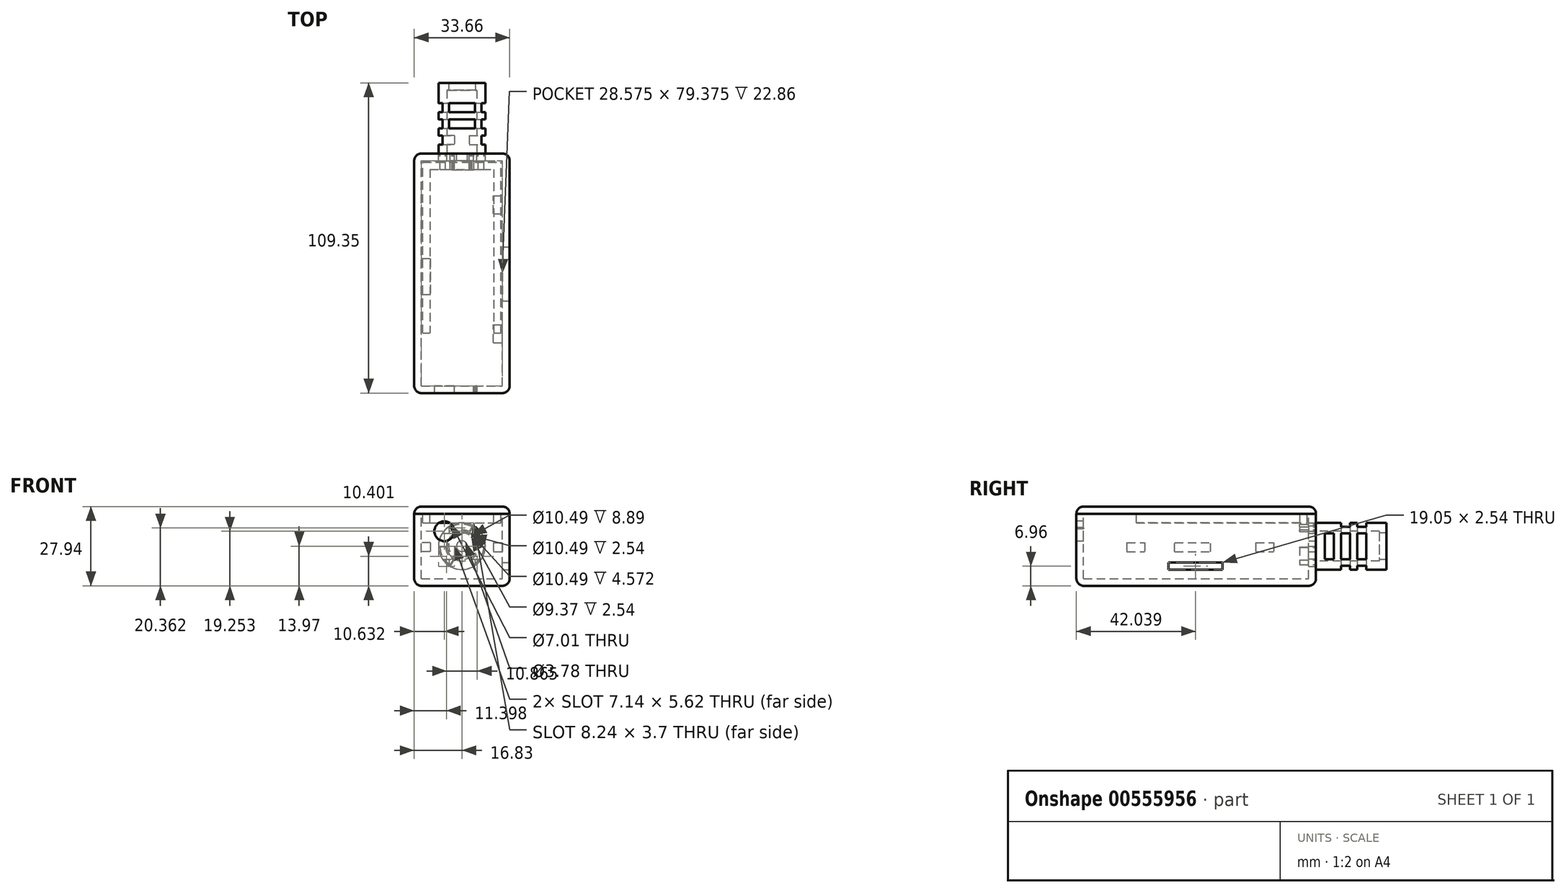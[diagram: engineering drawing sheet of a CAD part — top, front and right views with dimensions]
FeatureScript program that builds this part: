
annotation { "Feature Type Name" : "Feature", "Feature Type Description" : "" }
export const myFeature = defineFeature(function(context is Context, id is Id, definition is map)
    precondition{}
    {
        {
            var Q0;
            Q0=qCreatedBy(makeId("Top.planeOp"),FACE);
            var sketch = newSketch(context, id + "F0", { "sketchPlane" : qUnion([Q0])});
            skLineSegment(sketch, "E0.bottom", {"start": v(-14.29, -39.69) * mm, "end": v(14.29, -39.69) * mm});
            skLineSegment(sketch, "E0.top", {"start": v(-14.29, 39.69) * mm, "end": v(14.29, 39.69) * mm});
            skLineSegment(sketch, "E0.left", {"start": v(-14.29, -39.69) * mm, "end": v(-14.29, 39.69) * mm});
            skLineSegment(sketch, "E0.right", {"start": v(14.29, -39.69) * mm, "end": v(14.29, 39.69) * mm});
            skPoint(sketch, "E0.middle", {"position": v(0, 0) * mm});
            skLineSegment(sketch, "E1.0", {"start": v(-16.83, -42.23) * mm, "end": v(-16.83, 42.23) * mm});
            skLineSegment(sketch, "E1.1", {"start": v(-16.83, -42.23) * mm, "end": v(16.83, -42.23) * mm});
            skLineSegment(sketch, "E1.2", {"start": v(16.83, -42.23) * mm, "end": v(16.83, 42.23) * mm});
            skLineSegment(sketch, "E1.3", {"start": v(-16.83, 42.23) * mm, "end": v(16.83, 42.23) * mm});
            skSolve(sketch);
        }
        {
            var Q0;
            Q0=makeQuery(id+"F0.imprint","IMPRINT",FACE,{"disambiguationData":[TD([[makeQuery(id+"F0.imprint","IMPRINT",EDGE,{"derivedFrom":sQuery(id+"F0.wireOp",EDGE,"E0.bottom")}),1.0]])]});
            var Q1;
            Q1=makeQuery(id+"F0.imprint","IMPRINT",FACE,{"disambiguationData":[TD([[makeQuery(id+"F0.imprint","IMPRINT",EDGE,{"derivedFrom":sQuery(id+"F0.wireOp",EDGE,"E0.bottom")}),-1.0]])]});
            extrude(context, id + "F1", {"entities" : qUnion([Q0, Q1]), "depth" : 25.4 * mm, "offsetDistance" : 25.4 * mm});
        }
        {
            var Q0;
            Q0=makeQuery(id+"F1.opExtrude","CAP_FACE",FACE,{"disambiguationData":[OSD([sQuery(id+"F0.wireOp",EDGE,"E1.0"),sQuery(id+"F0.wireOp",EDGE,"E1.1"),sQuery(id+"F0.wireOp",EDGE,"E1.2"),sQuery(id+"F0.wireOp",EDGE,"E1.3")])],"isStart":false});
            var sketch = newSketch(context, id + "F2", { "sketchPlane" : qUnion([Q0])});
            skLineSegment(sketch, "E2.0", {"start": v(-14.29, 39.69) * mm, "end": v(14.29, 39.69) * mm});
            skLineSegment(sketch, "E3.0", {"start": v(14.29, -39.69) * mm, "end": v(14.29, 39.69) * mm});
            skLineSegment(sketch, "E4.0", {"start": v(-14.29, -39.69) * mm, "end": v(14.29, -39.69) * mm});
            skLineSegment(sketch, "E5.0", {"start": v(-14.29, -39.69) * mm, "end": v(-14.29, 39.69) * mm});
            skSolve(sketch);
        }
        {
            var Q0;
            Q0 = qSketchRegion(id + "F2", true);
            extrude(context, id + "F3", {"entities" : qUnion([Q0]), "operationType" : NewBodyOperationType.REMOVE, "oppositeDirection" : true, "depth" : 22.86 * mm, "offsetDistance" : 25.4 * mm});
        }
        {
            var Q0;
            Q0=makeQuery(id+"F1.opExtrude","SWEPT_FACE",FACE,{"disambiguationData":[OSD([sQuery(id+"F0.wireOp",EDGE,"E1.1")])]});
            var sketch = newSketch(context, id + "F4", { "sketchPlane" : qUnion([Q0])});
            skCircle(sketch, "E6", {"center": v(-6.2, 19.25) * mm, "radius": 3.5 * mm});
            skLineSegment(sketch, "E7", {"start": v(-16.83, 19.25) * mm, "end": v(-6.2, 19.25) * mm, "construction": true});
            skLineSegment(sketch, "E8", {"start": v(-6.2, 19.25) * mm, "end": v(-6.2, 0) * mm, "construction": true});
            skLineSegment(sketch, "E9", {"start": v(-16.83, 16.76) * mm, "end": v(16.83, 16.76) * mm, "construction": true});
            skLineSegment(sketch, "E10", {"start": v(0, 16.76) * mm, "end": v(0, 0) * mm, "construction": true});
            skLineSegment(sketch, "E11", {"start": v(5.8, 20.03) * mm, "end": v(8.1, 20.03) * mm});
            skPoint(sketch, "E12", {"position": v(5.8, 20.03) * mm});
            skLineSegment(sketch, "E13", {"start": v(6.32, 21.08) * mm, "end": v(8.95, 21.08) * mm});
            skPoint(sketch, "E14", {"position": v(6.32, 21.08) * mm});
            skLineSegment(sketch, "E15", {"start": v(6.32, 17.98) * mm, "end": v(8.44, 17.98) * mm});
            skPoint(sketch, "E16", {"position": v(6.32, 17.98) * mm});
            skLineSegment(sketch, "E17", {"start": v(6.32, 18.43) * mm, "end": v(8.07, 18.43) * mm});
            skPoint(sketch, "E18", {"position": v(6.32, 18.43) * mm});
            skPoint(sketch, "E19", {"position": v(5.8, 21.48) * mm});
            skPoint(sketch, "E20", {"position": v(5.8, 17.58) * mm});
            skArc(sketch, "E21", {"start": v(9.25, 20.78) * mm, "mid": v(9.17, 21) * mm, "end": v(8.95, 21.08) * mm});
            skLineSegment(sketch, "E22", {"start": v(9.25, 20.78) * mm, "end": v(9.25, 20.21) * mm});
            skArc(sketch, "E23", {"start": v(8.95, 19.64) * mm, "mid": v(9.17, 19.89) * mm, "end": v(9.25, 20.21) * mm});
            skArc(sketch, "E24", {"start": v(8.95, 19.64) * mm, "mid": v(8.8, 19.4) * mm, "end": v(8.74, 19.13) * mm});
            skArc(sketch, "E25", {"start": v(8.44, 17.98) * mm, "mid": v(8.65, 18.07) * mm, "end": v(8.74, 18.28) * mm});
            skLineSegment(sketch, "E26", {"start": v(8.74, 19.13) * mm, "end": v(8.74, 18.28) * mm});
            skLineSegment(sketch, "E27", {"start": v(8.1, 20.03) * mm, "end": v(8.1, 19.13) * mm});
            skLineSegment(sketch, "E28", {"start": v(8.1, 19.13) * mm, "end": v(8.07, 18.43) * mm});
            skLineSegment(sketch, "E29", {"start": v(5.8, 21.48) * mm, "end": v(5.8, 17.58) * mm, "construction": true});
            skLineSegment(sketch, "E30.bottom", {"start": v(7.15, 20.03) * mm, "end": v(7.65, 20.03) * mm});
            skLineSegment(sketch, "E30.top", {"start": v(7.15, 20.53) * mm, "end": v(7.65, 20.53) * mm});
            skLineSegment(sketch, "E30.left", {"start": v(7.15, 20.03) * mm, "end": v(7.15, 20.53) * mm});
            skLineSegment(sketch, "E30.right", {"start": v(7.65, 20.03) * mm, "end": v(7.65, 20.53) * mm});
            skPoint(sketch, "E30.middle", {"position": v(7.4, 20.28) * mm});
            skLineSegment(sketch, "E31.bottom", {"start": v(6.85, 20.03) * mm, "end": v(6.35, 20.03) * mm});
            skLineSegment(sketch, "E31.top", {"start": v(6.85, 20.53) * mm, "end": v(6.35, 20.53) * mm});
            skLineSegment(sketch, "E31.left", {"start": v(6.85, 20.03) * mm, "end": v(6.85, 20.53) * mm});
            skLineSegment(sketch, "E31.right", {"start": v(6.35, 20.03) * mm, "end": v(6.35, 20.53) * mm});
            skPoint(sketch, "E31.middle", {"position": v(6.6, 20.28) * mm});
            skLineSegment(sketch, "E32", {"start": v(6.05, 20.53) * mm, "end": v(6.05, 20.03) * mm});
            skLineSegment(sketch, "E33", {"start": v(6.32, 20.53) * mm, "end": v(6.05, 20.53) * mm});
            skLineSegment(sketch, "E34", {"start": v(5.8, 17.58) * mm, "end": v(8.44, 17.58) * mm});
            skLineSegment(sketch, "E35", {"start": v(5.8, 21.48) * mm, "end": v(8.95, 21.48) * mm});
            skArc(sketch, "E36", {"start": v(9.65, 20.78) * mm, "mid": v(9.45, 21.28) * mm, "end": v(8.95, 21.48) * mm});
            skLineSegment(sketch, "E37", {"start": v(9.65, 20.78) * mm, "end": v(9.65, 20.21) * mm});
            skArc(sketch, "E38", {"start": v(9.25, 19.36) * mm, "mid": v(9.55, 19.74) * mm, "end": v(9.65, 20.21) * mm});
            skArc(sketch, "E39", {"start": v(9.25, 19.36) * mm, "mid": v(9.17, 19.26) * mm, "end": v(9.14, 19.13) * mm});
            skLineSegment(sketch, "E40", {"start": v(9.14, 19.13) * mm, "end": v(9.14, 18.28) * mm});
            skArc(sketch, "E41", {"start": v(8.44, 17.58) * mm, "mid": v(8.94, 17.78) * mm, "end": v(9.14, 18.28) * mm});
            skArc(sketch, "E42.MirrorCS", {"start": v(2.35, 19.36) * mm, "mid": v(2.44, 19.26) * mm, "end": v(2.46, 19.13) * mm});
            skLineSegment(sketch, "E43.MirrorCS", {"start": v(4.45, 20.03) * mm, "end": v(3.95, 20.03) * mm});
            skLineSegment(sketch, "E44.MirrorCS", {"start": v(4.45, 20.03) * mm, "end": v(4.45, 20.53) * mm});
            skLineSegment(sketch, "E45.MirrorCS", {"start": v(4.75, 20.03) * mm, "end": v(5.25, 20.03) * mm});
            skLineSegment(sketch, "E46.MirrorCS", {"start": v(5.25, 20.03) * mm, "end": v(5.25, 20.53) * mm});
            skLineSegment(sketch, "E47.MirrorCS", {"start": v(5.55, 20.53) * mm, "end": v(5.55, 20.03) * mm});
            skLineSegment(sketch, "E48.MirrorCS", {"start": v(5.29, 20.53) * mm, "end": v(5.55, 20.53) * mm});
            skLineSegment(sketch, "E49.MirrorCS", {"start": v(4.45, 20.53) * mm, "end": v(3.95, 20.53) * mm});
            skArc(sketch, "E50.MirrorCS", {"start": v(3.17, 17.58) * mm, "mid": v(2.67, 17.78) * mm, "end": v(2.46, 18.28) * mm});
            skPoint(sketch, "E51.MirrorP", {"position": v(5.29, 18.43) * mm});
            skLineSegment(sketch, "E52.MirrorCS", {"start": v(5.29, 17.98) * mm, "end": v(3.17, 17.98) * mm});
            skLineSegment(sketch, "E53.MirrorCS", {"start": v(5.8, 21.48) * mm, "end": v(2.65, 21.48) * mm});
            skLineSegment(sketch, "E54.MirrorCS", {"start": v(5.29, 18.43) * mm, "end": v(3.53, 18.43) * mm});
            skPoint(sketch, "E55.MirrorP", {"position": v(4.2, 20.28) * mm});
            skArc(sketch, "E56.MirrorCS", {"start": v(1.95, 20.78) * mm, "mid": v(2.16, 21.28) * mm, "end": v(2.65, 21.48) * mm});
            skLineSegment(sketch, "E57.MirrorCS", {"start": v(4.75, 20.03) * mm, "end": v(4.75, 20.53) * mm});
            skPoint(sketch, "E58.MirrorP", {"position": v(5.29, 17.98) * mm});
            skLineSegment(sketch, "E59.MirrorCS", {"start": v(5.29, 21.08) * mm, "end": v(2.65, 21.08) * mm});
            skLineSegment(sketch, "E60.MirrorCS", {"start": v(3.5, 19.13) * mm, "end": v(3.53, 18.43) * mm});
            skLineSegment(sketch, "E61.MirrorCS", {"start": v(2.46, 19.13) * mm, "end": v(2.46, 18.28) * mm});
            skLineSegment(sketch, "E62.MirrorCS", {"start": v(4.75, 20.53) * mm, "end": v(5.25, 20.53) * mm});
            skArc(sketch, "E63.MirrorCS", {"start": v(2.35, 20.78) * mm, "mid": v(2.44, 21) * mm, "end": v(2.65, 21.08) * mm});
            skLineSegment(sketch, "E64.MirrorCS", {"start": v(1.95, 20.78) * mm, "end": v(1.95, 20.21) * mm});
            skArc(sketch, "E65.MirrorCS", {"start": v(2.65, 19.64) * mm, "mid": v(2.43, 19.89) * mm, "end": v(2.35, 20.21) * mm});
            skLineSegment(sketch, "E66.MirrorCS", {"start": v(5.8, 20.03) * mm, "end": v(3.5, 20.03) * mm});
            skLineSegment(sketch, "E67.MirrorCS", {"start": v(2.87, 19.13) * mm, "end": v(2.87, 18.28) * mm});
            skLineSegment(sketch, "E68.MirrorCS", {"start": v(3.5, 20.03) * mm, "end": v(3.5, 19.13) * mm});
            skLineSegment(sketch, "E69.MirrorCS", {"start": v(5.8, 17.58) * mm, "end": v(3.17, 17.58) * mm});
            skPoint(sketch, "E70.MirrorP", {"position": v(5.29, 21.08) * mm});
            skLineSegment(sketch, "E71.MirrorCS", {"start": v(2.35, 20.78) * mm, "end": v(2.35, 20.21) * mm});
            skArc(sketch, "E72.MirrorCS", {"start": v(3.17, 17.98) * mm, "mid": v(2.96, 18.07) * mm, "end": v(2.87, 18.28) * mm});
            skLineSegment(sketch, "E73.MirrorCS", {"start": v(3.95, 20.03) * mm, "end": v(3.95, 20.53) * mm});
            skPoint(sketch, "E74.MirrorP", {"position": v(5, 20.28) * mm});
            skArc(sketch, "E75.MirrorCS", {"start": v(2.35, 19.36) * mm, "mid": v(2.06, 19.74) * mm, "end": v(1.95, 20.21) * mm});
            skArc(sketch, "E76.MirrorCS", {"start": v(2.65, 19.64) * mm, "mid": v(2.81, 19.4) * mm, "end": v(2.87, 19.13) * mm});
            skLineSegment(sketch, "E77", {"start": v(-16.83, 18.75) * mm, "end": v(5.8, 18.75) * mm, "construction": true});
            skLineSegment(sketch, "E78", {"start": v(5.8, 19.53) * mm, "end": v(-16.83, 19.53) * mm, "construction": true});
            skLineSegment(sketch, "E79", {"start": v(5.8, 17.58) * mm, "end": v(5.8, 0) * mm, "construction": true});
            skSolve(sketch);
        }
        {
            var Q0;
            Q0=makeQuery(id+"F4.imprint","IMPRINT",FACE,{"disambiguationData":[TD([[makeQuery(id+"F4.imprint","IMPRINT",EDGE,{"derivedFrom":sQuery(id+"F4.wireOp",EDGE,"E6")}),1.0]])]});
            var Q1;
            Q1=makeQuery(id+"F4.imprint","IMPRINT",FACE,{"disambiguationData":[TD([[makeQuery(id+"F4.imprint","IMPRINT",EDGE,{"derivedFrom":sQuery(id+"F4.wireOp",EDGE,"E30.bottom")}),-1.0]])]});
            var Q2;
            {var subQ0=sQuery(id+"F4.wireOp",EDGE,"E46.MirrorCS");Q2=makeQuery(id+"F4.imprint","IMPRINT",FACE,{"disambiguationData":[TD([[makeQuery(id+"F4.imprint","IMPRINT",EDGE,{"derivedFrom":subQ0}),1.0]])]});}
            var Q3;
            Q3=makeQuery(id+"F4.imprint","IMPRINT",FACE,{"disambiguationData":[TD([[makeQuery(id+"F4.imprint","IMPRINT",EDGE,{"derivedFrom":sQuery(id+"F4.wireOp",EDGE,"E30.bottom")}),1.0]])]});
            var Q4;
            Q4=makeQuery(id+"F4.imprint","IMPRINT",FACE,{"disambiguationData":[TD([[makeQuery(id+"F4.imprint","IMPRINT",EDGE,{"derivedFrom":sQuery(id+"F4.wireOp",EDGE,"E31.bottom")}),-1.0]])]});
            var Q5;
            {var subQ0=sQuery(id+"F4.wireOp",EDGE,"E44.MirrorCS");Q5=makeQuery(id+"F4.imprint","IMPRINT",FACE,{"disambiguationData":[TD([[makeQuery(id+"F4.imprint","IMPRINT",EDGE,{"derivedFrom":subQ0}),1.0]])]});}
            extrude(context, id + "F5", {"entities" : qUnion([Q0, Q1, Q2, Q3, Q4, Q5]), "operationType" : NewBodyOperationType.REMOVE, "endBound" : BoundingType.UP_TO_NEXT, "oppositeDirection" : true, "depth" : 25.4 * mm, "offsetDistance" : 25.4 * mm});
        }
        {
            var Q0;
            Q0=makeQuery(id+"F1.opExtrude","SWEPT_FACE",FACE,{"disambiguationData":[OSD([sQuery(id+"F0.wireOp",EDGE,"E1.2")])]});
            var sketch = newSketch(context, id + "F6", { "sketchPlane" : qUnion([Q0])});
            skLineSegment(sketch, "E80", {"start": v(-42.23, 6.96) * mm, "end": v(-0.2, 6.96) * mm, "construction": true});
            skLineSegment(sketch, "E81", {"start": v(-17.06, 6.96) * mm, "end": v(-17.06, 0) * mm, "construction": true});
            skLineSegment(sketch, "E82.bottom", {"start": v(9.33, 5.69) * mm, "end": v(-9.72, 5.69) * mm});
            skLineSegment(sketch, "E82.top", {"start": v(9.33, 8.23) * mm, "end": v(-9.72, 8.23) * mm});
            skLineSegment(sketch, "E82.left", {"start": v(9.33, 5.69) * mm, "end": v(9.33, 8.23) * mm});
            skLineSegment(sketch, "E82.right", {"start": v(-9.72, 5.69) * mm, "end": v(-9.72, 8.23) * mm});
            skPoint(sketch, "E82.middle", {"position": v(-0.2, 6.96) * mm});
            skLineSegment(sketch, "E83", {"start": v(-42.23, 15.16) * mm, "end": v(42.23, 15.16) * mm, "construction": true});
            skLineSegment(sketch, "E84", {"start": v(-0.2, 6.96) * mm, "end": v(-0.2, 15.16) * mm, "construction": true});
            skLineSegment(sketch, "E85.bottom", {"start": v(-24.44, 15.16) * mm, "end": v(-18.09, 15.16) * mm});
            skLineSegment(sketch, "E85.top", {"start": v(-24.44, 11.99) * mm, "end": v(-18.09, 11.99) * mm});
            skLineSegment(sketch, "E85.left", {"start": v(-24.44, 15.16) * mm, "end": v(-24.44, 11.99) * mm});
            skLineSegment(sketch, "E85.right", {"start": v(-18.09, 15.16) * mm, "end": v(-18.09, 11.99) * mm});
            skLineSegment(sketch, "E86.bottom", {"start": v(20.98, 15.16) * mm, "end": v(27.33, 15.16) * mm});
            skLineSegment(sketch, "E86.top", {"start": v(20.98, 11.99) * mm, "end": v(27.33, 11.99) * mm});
            skLineSegment(sketch, "E86.left", {"start": v(20.98, 15.16) * mm, "end": v(20.98, 11.99) * mm});
            skLineSegment(sketch, "E86.right", {"start": v(27.33, 15.16) * mm, "end": v(27.33, 11.99) * mm});
            skLineSegment(sketch, "E87", {"start": v(15.27, 15.16) * mm, "end": v(15.27, 0) * mm, "construction": true});
            skSolve(sketch);
        }
        {
            var Q0;
            Q0=makeQuery(id+"F6.imprint","IMPRINT",FACE,{"disambiguationData":[TD([[makeQuery(id+"F6.imprint","IMPRINT",EDGE,{"derivedFrom":sQuery(id+"F6.wireOp",EDGE,"E82.bottom")}),-1.0]])]});
            extrude(context, id + "F7", {"entities" : qUnion([Q0]), "operationType" : NewBodyOperationType.REMOVE, "oppositeDirection" : true, "depth" : 5.08 * mm, "offsetDistance" : 25.4 * mm});
        }
        {
            var Q0;
            Q0=makeQuery(id+"F2.imprint","IMPRINT",FACE,{"disambiguationData":[TD([[makeQuery(id+"F2.imprint","IMPRINT",EDGE,{"derivedFrom":sQuery(id+"F2.wireOp",EDGE,"E2.0")}),-1.0]])]});
            var sketch = newSketch(context, id + "F8", { "sketchPlane" : qUnion([Q0])});
            skLineSegment(sketch, "E88.0", {"start": v(-16.83, 42.23) * mm, "end": v(16.83, 42.23) * mm});
            skLineSegment(sketch, "E89.0", {"start": v(16.83, -42.23) * mm, "end": v(16.83, 42.23) * mm});
            skPoint(sketch, "E90.0", {"position": v(0, -42.23) * mm});
            skLineSegment(sketch, "E91.0", {"start": v(-16.83, -42.23) * mm, "end": v(-16.83, 42.23) * mm});
            skLineSegment(sketch, "E92.0", {"start": v(-14.29, -39.69) * mm, "end": v(-14.29, 39.69) * mm});
            skLineSegment(sketch, "E93.0", {"start": v(-14.29, 39.69) * mm, "end": v(14.29, 39.69) * mm});
            skLineSegment(sketch, "E94.0", {"start": v(14.29, -39.69) * mm, "end": v(14.29, 39.69) * mm});
            skLineSegment(sketch, "E95.0", {"start": v(-14.29, -39.69) * mm, "end": v(14.29, -39.69) * mm});
            skLineSegment(sketch, "E96.0", {"start": v(-13.78, 39.18) * mm, "end": v(13.78, 39.18) * mm});
            skLineSegment(sketch, "E96.1", {"start": v(-13.78, -39.18) * mm, "end": v(-13.78, 39.18) * mm});
            skLineSegment(sketch, "E96.2", {"start": v(-13.78, -39.18) * mm, "end": v(13.78, -39.18) * mm});
            skLineSegment(sketch, "E96.3", {"start": v(13.78, -39.18) * mm, "end": v(13.78, 39.18) * mm});
            skLineSegment(sketch, "E97.0.0", {"start": v(-14.29, 39.69) * mm, "end": v(-14.29, -39.69) * mm});
            skLineSegment(sketch, "E97.0.3", {"start": v(14.29, 39.69) * mm, "end": v(-14.29, 39.69) * mm});
            skSolve(sketch);
        }
        {
            var Q0;
            Q0=makeQuery(id+"F2.imprint","IMPRINT",FACE,{"disambiguationData":[TD([[makeQuery(id+"F2.imprint","IMPRINT",EDGE,{"derivedFrom":sQuery(id+"F2.wireOp",EDGE,"E2.0")}),1.0]])]});
            var Q1;
            Q1=makeQuery(id+"F2.imprint","IMPRINT",FACE,{"disambiguationData":[TD([[makeQuery(id+"F2.imprint","IMPRINT",EDGE,{"derivedFrom":sQuery(id+"F2.wireOp",EDGE,"E2.0")}),-1.0]])]});
            extrude(context, id + "F9", {"entities" : qUnion([Q0, Q1]), "depth" : 2.54 * mm, "offsetDistance" : 25.4 * mm});
        }
        {
            var Q0;
            Q0=makeQuery(id+"F8.imprint","IMPRINT",FACE,{"disambiguationData":[TD([[makeQuery(id+"F8.imprint","IMPRINT",EDGE,{"derivedFrom":sQuery(id+"F8.wireOp",EDGE,"E96.0")}),-1.0]])]});
            var sketch = newSketch(context, id + "F10", { "sketchPlane" : qUnion([Q0])});
            skLineSegment(sketch, "E98.0", {"start": v(11.24, -39.18) * mm, "end": v(11.24, 36.64) * mm, "construction": true});
            skLineSegment(sketch, "E98.1", {"start": v(-11.24, 36.64) * mm, "end": v(11.24, 36.64) * mm, "construction": true});
            skLineSegment(sketch, "E98.2", {"start": v(-11.24, -39.18) * mm, "end": v(-11.24, 36.64) * mm, "construction": true});
            skLineSegment(sketch, "E99.0", {"start": v(-13.78, 39.18) * mm, "end": v(13.78, 39.18) * mm, "construction": true});
            skLineSegment(sketch, "E100.0", {"start": v(-13.78, -39.18) * mm, "end": v(-13.78, 39.18) * mm, "construction": true});
            skLineSegment(sketch, "E101.0", {"start": v(13.78, -39.18) * mm, "end": v(13.78, 39.18) * mm, "construction": true});
            skLineSegment(sketch, "E102", {"start": v(-16.83, -21.1) * mm, "end": v(16.83, -21.1) * mm, "construction": true});
            skLineSegment(sketch, "E103", {"start": v(-13.78, -21.1) * mm, "end": v(-11.24, -21.1) * mm});
            skLineSegment(sketch, "E104", {"start": v(11.24, -21.1) * mm, "end": v(13.78, -21.1) * mm});
            skLineSegment(sketch, "E105", {"start": v(-13.78, 39.18) * mm, "end": v(-13.78, -21.1) * mm});
            skLineSegment(sketch, "E106", {"start": v(-11.24, 36.64) * mm, "end": v(-11.24, -21.1) * mm});
            skLineSegment(sketch, "E107", {"start": v(-13.78, 39.18) * mm, "end": v(13.78, 39.18) * mm});
            skLineSegment(sketch, "E108", {"start": v(-11.24, 36.64) * mm, "end": v(11.24, 36.64) * mm});
            skLineSegment(sketch, "E109", {"start": v(11.24, 36.64) * mm, "end": v(11.24, -21.1) * mm});
            skLineSegment(sketch, "E110", {"start": v(13.78, 39.18) * mm, "end": v(13.78, -21.1) * mm});
            skSolve(sketch);
        }
        {
            var Q0;
            Q0=makeQuery(id+"F10.imprint","IMPRINT",FACE,{"disambiguationData":[TD([[makeQuery(id+"F10.imprint","IMPRINT",EDGE,{"derivedFrom":sQuery(id+"F10.wireOp",EDGE,"E103")}),1.0]])]});
            var Q1;
            Q1=sQuery(id+"F10.wireOp",EDGE,"E105");
            var Q2;
            Q2=sQuery(id+"F10.wireOp",EDGE,"E107");
            var Q3;
            Q3=sQuery(id+"F10.wireOp",EDGE,"E110");
            var Q4;
            Q4=sQuery(id+"F10.wireOp",EDGE,"E103");
            var Q5;
            Q5=sQuery(id+"F10.wireOp",EDGE,"E106");
            var Q6;
            Q6=sQuery(id+"F10.wireOp",EDGE,"E104");
            var Q7;
            Q7=sQuery(id+"F10.wireOp",EDGE,"E109");
            var Q8;
            Q8=sQuery(id+"F10.wireOp",EDGE,"E108");
            extrude(context, id + "F11", {"entities" : qUnion([Q0]), "operationType" : NewBodyOperationType.ADD, "surfaceEntities" : qUnion([Q1, Q2, Q3, Q4, Q5, Q6, Q7, Q8]), "oppositeDirection" : true, "depth" : 3.17 * mm, "offsetDistance" : 25.4 * mm});
        }
        {
            var Q0;
            Q0=makeQuery(id+"F6.imprint","IMPRINT",FACE,{"disambiguationData":[TD([[makeQuery(id+"F6.imprint","IMPRINT",EDGE,{"derivedFrom":sQuery(id+"F6.wireOp",EDGE,"E86.bottom")}),-1.0]])]});
            var Q1;
            Q1=makeQuery(id+"F6.imprint","IMPRINT",FACE,{"disambiguationData":[TD([[makeQuery(id+"F6.imprint","IMPRINT",EDGE,{"derivedFrom":sQuery(id+"F6.wireOp",EDGE,"E85.bottom")}),-1.0]])]});
            extrude(context, id + "F12", {"entities" : qUnion([Q0, Q1]), "operationType" : NewBodyOperationType.ADD, "oppositeDirection" : true, "depth" : 5.7 * mm, "offsetDistance" : 25.4 * mm});
        }
        {
            var Q0;
            Q0=makeQuery(id+"F1.opExtrude","SWEPT_FACE",FACE,{"disambiguationData":[OSD([sQuery(id+"F0.wireOp",EDGE,"E1.0")])]});
            var sketch = newSketch(context, id + "F13", { "sketchPlane" : qUnion([Q0])});
            skLineSegment(sketch, "E111.bottom", {"start": v(-5.13, 15.16) * mm, "end": v(7.57, 15.16) * mm});
            skLineSegment(sketch, "E111.top", {"start": v(-5.13, 11.99) * mm, "end": v(7.57, 11.99) * mm});
            skLineSegment(sketch, "E111.left", {"start": v(-5.13, 15.16) * mm, "end": v(-5.13, 11.99) * mm});
            skLineSegment(sketch, "E111.right", {"start": v(7.57, 15.16) * mm, "end": v(7.57, 11.99) * mm});
            skLineSegment(sketch, "E112", {"start": v(-1.66, 15.16) * mm, "end": v(-1.66, 0) * mm, "construction": true});
            skSolve(sketch);
        }
        {
            var Q0;
            Q0=makeQuery(id+"F13.imprint","IMPRINT",FACE,{"disambiguationData":[TD([[makeQuery(id+"F13.imprint","IMPRINT",EDGE,{"derivedFrom":sQuery(id+"F13.wireOp",EDGE,"E111.bottom")}),-1.0]])]});
            extrude(context, id + "F14", {"entities" : qUnion([Q0]), "operationType" : NewBodyOperationType.ADD, "oppositeDirection" : true, "depth" : 5.7 * mm, "offsetDistance" : 25.4 * mm});
        }
        {
            var Q0;
            Q0=makeQuery(id+"F1.opExtrude","SWEPT_FACE",FACE,{"disambiguationData":[OSD([sQuery(id+"F0.wireOp",EDGE,"E1.3")])]});
            var sketch = newSketch(context, id + "F15", { "sketchPlane" : qUnion([Q0])});
            skLineSegment(sketch, "E113", {"start": v(-16.83, 15.16) * mm, "end": v(16.83, 15.16) * mm, "construction": true});
            skLineSegment(sketch, "E114", {"start": v(7.72, 15.16) * mm, "end": v(7.72, 0) * mm, "construction": true});
            skCircle(sketch, "E115", {"center": v(0, 13.97) * mm, "radius": 5.25 * mm});
            skLineSegment(sketch, "E116", {"start": v(-16.83, 16.76) * mm, "end": v(16.83, 16.76) * mm, "construction": true});
            skLineSegment(sketch, "E117", {"start": v(10.95, 16.76) * mm, "end": v(10.95, 0) * mm, "construction": true});
            skLineSegment(sketch, "E118", {"start": v(-16.83, 25.4) * mm, "end": v(-16.83, 0) * mm, "construction": true});
            skLineSegment(sketch, "E119", {"start": v(0, 13.97) * mm, "end": v(0, 0) * mm, "construction": true});
            skCircle(sketch, "E120.0", {"center": v(0, 13.97) * mm, "radius": 8.24 * mm});
            skLineSegment(sketch, "E121", {"start": v(0, 13.97) * mm, "end": v(0, 22.21) * mm, "construction": true});
            skLineSegment(sketch, "E122", {"start": v(0, 13.97) * mm, "end": v(-4.12, 21.1) * mm, "construction": true});
            skLineSegment(sketch, "E123", {"start": v(0, 13.97) * mm, "end": v(4.12, 21.1) * mm, "construction": true});
            skLineSegment(sketch, "E124", {"start": v(0, 13.97) * mm, "end": v(8.24, 13.97) * mm, "construction": true});
            skLineSegment(sketch, "E125", {"start": v(0, 13.97) * mm, "end": v(4.12, 6.83) * mm, "construction": true});
            skLineSegment(sketch, "E126", {"start": v(0, 13.97) * mm, "end": v(-8.24, 13.97) * mm, "construction": true});
            skLineSegment(sketch, "E127", {"start": v(0, 13.97) * mm, "end": v(-4.12, 6.83) * mm, "construction": true});
            skLineSegment(sketch, "E128", {"start": v(-4.12, 21.1) * mm, "end": v(-2.62, 18.51) * mm});
            skLineSegment(sketch, "E129", {"start": v(4.12, 21.1) * mm, "end": v(2.62, 18.51) * mm});
            skLineSegment(sketch, "E130", {"start": v(8.24, 13.97) * mm, "end": v(5.25, 13.97) * mm});
            skLineSegment(sketch, "E131", {"start": v(2.62, 9.43) * mm, "end": v(4.12, 6.83) * mm});
            skLineSegment(sketch, "E132", {"start": v(-4.12, 6.83) * mm, "end": v(-2.62, 9.43) * mm});
            skLineSegment(sketch, "E133", {"start": v(-5.25, 13.97) * mm, "end": v(-8.24, 13.97) * mm});
            skCircle(sketch, "E134", {"center": v(0, 13.97) * mm, "radius": 1 * mm});
            skCircle(sketch, "E135.0", {"center": v(0, 13.97) * mm, "radius": 1.9 * mm});
            skCircle(sketch, "E136.0", {"center": v(0, 13.97) * mm, "radius": 7.73 * mm});
            skCircle(sketch, "E137.0", {"center": v(0, 13.97) * mm, "radius": 5.75 * mm});
            skLineSegment(sketch, "E138", {"start": v(-3.77, 21.3) * mm, "end": v(0, 13.97) * mm, "construction": true});
            skLineSegment(sketch, "E139", {"start": v(3.77, 21.3) * mm, "end": v(0, 13.97) * mm, "construction": true});
            skLineSegment(sketch, "E140", {"start": v(0, 13.97) * mm, "end": v(8.23, 13.57) * mm, "construction": true});
            skLineSegment(sketch, "E141", {"start": v(0, 13.97) * mm, "end": v(4.46, 7.04) * mm, "construction": true});
            skLineSegment(sketch, "E142", {"start": v(0, 13.97) * mm, "end": v(-4.46, 7.04) * mm, "construction": true});
            skLineSegment(sketch, "E143", {"start": v(0, 13.97) * mm, "end": v(-8.23, 13.57) * mm, "construction": true});
            skLineSegment(sketch, "E144", {"start": v(-3.54, 20.85) * mm, "end": v(-2.63, 19.09) * mm});
            skLineSegment(sketch, "E145", {"start": v(3.54, 20.85) * mm, "end": v(2.63, 19.09) * mm});
            skLineSegment(sketch, "E146", {"start": v(-7.73, 13.6) * mm, "end": v(-5.75, 13.7) * mm});
            skLineSegment(sketch, "E147", {"start": v(-3.11, 9.13) * mm, "end": v(-4.19, 7.47) * mm});
            skLineSegment(sketch, "E148", {"start": v(3.11, 9.13) * mm, "end": v(4.19, 7.47) * mm});
            skLineSegment(sketch, "E149", {"start": v(5.75, 13.7) * mm, "end": v(7.73, 13.6) * mm});
            skLineSegment(sketch, "E150", {"start": v(-4.46, 7.04) * mm, "end": v(-2.84, 9.56) * mm});
            skLineSegment(sketch, "E151", {"start": v(4.46, 7.04) * mm, "end": v(2.84, 9.56) * mm});
            skSolve(sketch);
        }
        {
            var Q0;
            {var subQ4=sQuery(id+"F15.wireOp",EDGE,"E128");var subQ5=sQuery(id+"F15.wireOp",EDGE,"E120.0");var subQ6=makeQuery(id+"F15.imprint","INTERSECT",VERTEX,{"derivedFrom":[subQ5,subQ4]});Q0=makeQuery(id+"F15.imprint","IMPRINT",FACE,{"disambiguationData":[TD([[makeQuery(id+"F15.imprint","IMPRINT",EDGE,{"disambiguationData":[TD([[subQ6,1.0]])],"derivedFrom":subQ5}),1.0]])]});}
            var Q1;
            {var subQ0=sQuery(id+"F15.wireOp",EDGE,"E144");Q1=makeQuery(id+"F15.imprint","IMPRINT",FACE,{"disambiguationData":[TD([[makeQuery(id+"F15.imprint","IMPRINT",EDGE,{"derivedFrom":subQ0}),1.0]])]});}
            var Q2;
            {var subQ5=sQuery(id+"F15.wireOp",EDGE,"E144");Q2=makeQuery(id+"F15.imprint","IMPRINT",FACE,{"disambiguationData":[TD([[makeQuery(id+"F15.imprint","IMPRINT",EDGE,{"derivedFrom":subQ5}),-1.0]])]});}
            var Q3;
            {var subQ5=sQuery(id+"F15.wireOp",EDGE,"E145");Q3=makeQuery(id+"F15.imprint","IMPRINT",FACE,{"disambiguationData":[TD([[makeQuery(id+"F15.imprint","IMPRINT",EDGE,{"derivedFrom":subQ5}),1.0]])]});}
            var Q4;
            {var subQ4=sQuery(id+"F15.wireOp",EDGE,"E128");var subQ5=sQuery(id+"F15.wireOp",EDGE,"E115");var subQ6=makeQuery(id+"F15.imprint","INTERSECT",VERTEX,{"derivedFrom":[subQ5,subQ4]});Q4=makeQuery(id+"F15.imprint","IMPRINT",FACE,{"disambiguationData":[TD([[makeQuery(id+"F15.imprint","IMPRINT",EDGE,{"disambiguationData":[TD([[subQ6,1.0]])],"derivedFrom":subQ5}),-1.0]])]});}
            var Q5;
            {var subQ4=sQuery(id+"F15.wireOp",EDGE,"E130");var subQ6=sQuery(id+"F15.wireOp",EDGE,"E120.0");var subQ7=makeQuery(id+"F15.imprint","INTERSECT",VERTEX,{"derivedFrom":[subQ6,subQ4]});Q5=makeQuery(id+"F15.imprint","IMPRINT",FACE,{"disambiguationData":[TD([[makeQuery(id+"F15.imprint","IMPRINT",EDGE,{"disambiguationData":[TD([[subQ7,1.0]])],"derivedFrom":subQ6}),1.0]])]});}
            var Q6;
            {var subQ0=sQuery(id+"F15.wireOp",EDGE,"E131");var subQ1=sQuery(id+"F15.wireOp",EDGE,"E120.0");var subQ2=makeQuery(id+"F15.imprint","INTERSECT",VERTEX,{"derivedFrom":[subQ1,subQ0]});Q6=makeQuery(id+"F15.imprint","IMPRINT",FACE,{"disambiguationData":[TD([[makeQuery(id+"F15.imprint","IMPRINT",EDGE,{"disambiguationData":[TD([[subQ2,-1.0]])],"derivedFrom":subQ1}),1.0]])]});}
            var Q7;
            {var subQ5=sQuery(id+"F15.wireOp",EDGE,"E149");Q7=makeQuery(id+"F15.imprint","IMPRINT",FACE,{"disambiguationData":[TD([[makeQuery(id+"F15.imprint","IMPRINT",EDGE,{"derivedFrom":subQ5}),1.0]])]});}
            var Q8;
            {var subQ0=sQuery(id+"F15.wireOp",EDGE,"E149");Q8=makeQuery(id+"F15.imprint","IMPRINT",FACE,{"disambiguationData":[TD([[makeQuery(id+"F15.imprint","IMPRINT",EDGE,{"derivedFrom":subQ0}),-1.0]])]});}
            var Q9;
            {var subQ0=sQuery(id+"F15.wireOp",EDGE,"E137.0");var subQ1=sQuery(id+"F15.wireOp",EDGE,"E131");var subQ2=makeQuery(id+"F15.imprint","INTERSECT",VERTEX,{"derivedFrom":[subQ1,subQ0]});Q9=makeQuery(id+"F15.imprint","IMPRINT",FACE,{"disambiguationData":[TD([[makeQuery(id+"F15.imprint","IMPRINT",EDGE,{"disambiguationData":[TD([[subQ2,-1.0]])],"derivedFrom":subQ1}),1.0]])]});}
            var Q10;
            {var subQ4=sQuery(id+"F15.wireOp",EDGE,"E115");var subQ6=sQuery(id+"F15.wireOp",EDGE,"E130");var subQ8=makeQuery(id+"F15.imprint","INTERSECT",VERTEX,{"derivedFrom":[subQ4,subQ6]});Q10=makeQuery(id+"F15.imprint","IMPRINT",FACE,{"disambiguationData":[TD([[makeQuery(id+"F15.imprint","IMPRINT",EDGE,{"disambiguationData":[TD([[subQ8,1.0]])],"derivedFrom":subQ4}),-1.0]])]});}
            var Q11;
            {var subQ0=sQuery(id+"F15.wireOp",EDGE,"E131");var subQ1=sQuery(id+"F15.wireOp",EDGE,"E115");var subQ2=makeQuery(id+"F15.imprint","INTERSECT",VERTEX,{"derivedFrom":[subQ1,subQ0]});Q11=makeQuery(id+"F15.imprint","IMPRINT",FACE,{"disambiguationData":[TD([[makeQuery(id+"F15.imprint","IMPRINT",EDGE,{"disambiguationData":[TD([[subQ2,-1.0]])],"derivedFrom":subQ1}),-1.0]])]});}
            var Q12;
            {var subQ0=sQuery(id+"F15.wireOp",EDGE,"E146");Q12=makeQuery(id+"F15.imprint","IMPRINT",FACE,{"disambiguationData":[TD([[makeQuery(id+"F15.imprint","IMPRINT",EDGE,{"derivedFrom":subQ0}),-1.0]])]});}
            var Q13;
            {var subQ4=sQuery(id+"F15.wireOp",EDGE,"E133");var subQ5=sQuery(id+"F15.wireOp",EDGE,"E115");var subQ6=makeQuery(id+"F15.imprint","INTERSECT",VERTEX,{"derivedFrom":[subQ5,subQ4]});Q13=makeQuery(id+"F15.imprint","IMPRINT",FACE,{"disambiguationData":[TD([[makeQuery(id+"F15.imprint","IMPRINT",EDGE,{"disambiguationData":[TD([[subQ6,-1.0]])],"derivedFrom":subQ5}),-1.0]])]});}
            var Q14;
            {var subQ5=sQuery(id+"F15.wireOp",EDGE,"E146");Q14=makeQuery(id+"F15.imprint","IMPRINT",FACE,{"disambiguationData":[TD([[makeQuery(id+"F15.imprint","IMPRINT",EDGE,{"derivedFrom":subQ5}),1.0]])]});}
            var Q15;
            {var subQ4=sQuery(id+"F15.wireOp",EDGE,"E120.0");var subQ6=sQuery(id+"F15.wireOp",EDGE,"E133");var subQ7=makeQuery(id+"F15.imprint","INTERSECT",VERTEX,{"derivedFrom":[subQ4,subQ6]});Q15=makeQuery(id+"F15.imprint","IMPRINT",FACE,{"disambiguationData":[TD([[makeQuery(id+"F15.imprint","IMPRINT",EDGE,{"disambiguationData":[TD([[subQ7,-1.0]])],"derivedFrom":subQ4}),1.0]])]});}
            var Q16;
            {var subQ0=sQuery(id+"F15.wireOp",EDGE,"E132");var subQ1=sQuery(id+"F15.wireOp",EDGE,"E115");var subQ2=makeQuery(id+"F15.imprint","INTERSECT",VERTEX,{"derivedFrom":[subQ1,subQ0]});Q16=makeQuery(id+"F15.imprint","IMPRINT",FACE,{"disambiguationData":[TD([[makeQuery(id+"F15.imprint","IMPRINT",EDGE,{"disambiguationData":[TD([[subQ2,1.0]])],"derivedFrom":subQ1}),-1.0]])]});}
            var Q17;
            {var subQ0=sQuery(id+"F15.wireOp",EDGE,"E136.0");var subQ1=sQuery(id+"F15.wireOp",EDGE,"E132");var subQ2=makeQuery(id+"F15.imprint","INTERSECT",VERTEX,{"derivedFrom":[subQ1,subQ0]});Q17=makeQuery(id+"F15.imprint","IMPRINT",FACE,{"disambiguationData":[TD([[makeQuery(id+"F15.imprint","IMPRINT",EDGE,{"disambiguationData":[TD([[subQ2,-1.0]])],"derivedFrom":subQ1}),1.0]])]});}
            var Q18;
            {var subQ0=sQuery(id+"F15.wireOp",EDGE,"E132");var subQ1=sQuery(id+"F15.wireOp",EDGE,"E120.0");var subQ2=makeQuery(id+"F15.imprint","INTERSECT",VERTEX,{"derivedFrom":[subQ1,subQ0]});Q18=makeQuery(id+"F15.imprint","IMPRINT",FACE,{"disambiguationData":[TD([[makeQuery(id+"F15.imprint","IMPRINT",EDGE,{"disambiguationData":[TD([[subQ2,1.0]])],"derivedFrom":subQ1}),1.0]])]});}
            var Q19;
            Q19=makeQuery(id+"F15.imprint","IMPRINT",FACE,{"disambiguationData":[TD([[makeQuery(id+"F15.imprint","IMPRINT",EDGE,{"derivedFrom":sQuery(id+"F15.wireOp",EDGE,"E134")}),1.0]])]});
            var Q20;
            Q20=makeQuery(id+"F15.imprint","IMPRINT",FACE,{"disambiguationData":[TD([[makeQuery(id+"F15.imprint","IMPRINT",EDGE,{"derivedFrom":sQuery(id+"F15.wireOp",EDGE,"E134")}),-1.0]])]});
            extrude(context, id + "F16", {"entities" : qUnion([Q0, Q1, Q2, Q3, Q4, Q5, Q6, Q7, Q8, Q9, Q10, Q11, Q12, Q13, Q14, Q15, Q16, Q17, Q18, Q19, Q20]), "operationType" : NewBodyOperationType.REMOVE, "endBound" : BoundingType.UP_TO_NEXT, "oppositeDirection" : true, "depth" : 25.4 * mm, "offsetDistance" : 25.4 * mm});
        }
        {
            var Q0;
            {var subQ0=sQuery(id+"F15.wireOp",EDGE,"E144");Q0=makeQuery(id+"F15.imprint","IMPRINT",FACE,{"disambiguationData":[TD([[makeQuery(id+"F15.imprint","IMPRINT",EDGE,{"derivedFrom":subQ0}),1.0]])]});}
            var Q1;
            {var subQ0=sQuery(id+"F15.wireOp",EDGE,"E136.0");var subQ1=sQuery(id+"F15.wireOp",EDGE,"E128");var subQ2=makeQuery(id+"F15.imprint","INTERSECT",VERTEX,{"derivedFrom":[subQ1,subQ0]});Q1=makeQuery(id+"F15.imprint","IMPRINT",FACE,{"disambiguationData":[TD([[makeQuery(id+"F15.imprint","IMPRINT",EDGE,{"disambiguationData":[TD([[subQ2,-1.0]])],"derivedFrom":subQ1}),-1.0]])]});}
            var Q2;
            {var subQ5=sQuery(id+"F15.wireOp",EDGE,"E144");Q2=makeQuery(id+"F15.imprint","IMPRINT",FACE,{"disambiguationData":[TD([[makeQuery(id+"F15.imprint","IMPRINT",EDGE,{"derivedFrom":subQ5}),-1.0]])]});}
            var Q3;
            {var subQ4=sQuery(id+"F15.wireOp",EDGE,"E128");var subQ5=sQuery(id+"F15.wireOp",EDGE,"E120.0");var subQ6=makeQuery(id+"F15.imprint","INTERSECT",VERTEX,{"derivedFrom":[subQ5,subQ4]});Q3=makeQuery(id+"F15.imprint","IMPRINT",FACE,{"disambiguationData":[TD([[makeQuery(id+"F15.imprint","IMPRINT",EDGE,{"disambiguationData":[TD([[subQ6,1.0]])],"derivedFrom":subQ5}),1.0]])]});}
            var Q4;
            {var subQ0=sQuery(id+"F15.wireOp",EDGE,"E128");var subQ1=sQuery(id+"F15.wireOp",EDGE,"E120.0");var subQ2=makeQuery(id+"F15.imprint","INTERSECT",VERTEX,{"derivedFrom":[subQ1,subQ0]});Q4=makeQuery(id+"F15.imprint","IMPRINT",FACE,{"disambiguationData":[TD([[makeQuery(id+"F15.imprint","IMPRINT",EDGE,{"disambiguationData":[TD([[subQ2,-1.0]])],"derivedFrom":subQ1}),1.0]])]});}
            var Q5;
            {var subQ4=sQuery(id+"F15.wireOp",EDGE,"E128");var subQ5=sQuery(id+"F15.wireOp",EDGE,"E115");var subQ6=makeQuery(id+"F15.imprint","INTERSECT",VERTEX,{"derivedFrom":[subQ5,subQ4]});Q5=makeQuery(id+"F15.imprint","IMPRINT",FACE,{"disambiguationData":[TD([[makeQuery(id+"F15.imprint","IMPRINT",EDGE,{"disambiguationData":[TD([[subQ6,1.0]])],"derivedFrom":subQ5}),-1.0]])]});}
            var Q6;
            {var subQ0=sQuery(id+"F15.wireOp",EDGE,"E128");var subQ1=sQuery(id+"F15.wireOp",EDGE,"E115");var subQ2=makeQuery(id+"F15.imprint","INTERSECT",VERTEX,{"derivedFrom":[subQ1,subQ0]});Q6=makeQuery(id+"F15.imprint","IMPRINT",FACE,{"disambiguationData":[TD([[makeQuery(id+"F15.imprint","IMPRINT",EDGE,{"disambiguationData":[TD([[subQ2,-1.0]])],"derivedFrom":subQ1}),-1.0]])]});}
            var Q7;
            {var subQ0=sQuery(id+"F15.wireOp",EDGE,"E136.0");var subQ1=sQuery(id+"F15.wireOp",EDGE,"E129");var subQ2=makeQuery(id+"F15.imprint","INTERSECT",VERTEX,{"derivedFrom":[subQ1,subQ0]});Q7=makeQuery(id+"F15.imprint","IMPRINT",FACE,{"disambiguationData":[TD([[makeQuery(id+"F15.imprint","IMPRINT",EDGE,{"disambiguationData":[TD([[subQ2,-1.0]])],"derivedFrom":subQ1}),1.0]])]});}
            var Q8;
            {var subQ0=sQuery(id+"F15.wireOp",EDGE,"E129");var subQ1=sQuery(id+"F15.wireOp",EDGE,"E120.0");var subQ2=makeQuery(id+"F15.imprint","INTERSECT",VERTEX,{"derivedFrom":[subQ1,subQ0]});Q8=makeQuery(id+"F15.imprint","IMPRINT",FACE,{"disambiguationData":[TD([[makeQuery(id+"F15.imprint","IMPRINT",EDGE,{"disambiguationData":[TD([[subQ2,1.0]])],"derivedFrom":subQ1}),1.0]])]});}
            var Q9;
            {var subQ0=sQuery(id+"F15.wireOp",EDGE,"E129");var subQ1=sQuery(id+"F15.wireOp",EDGE,"E115");var subQ2=makeQuery(id+"F15.imprint","INTERSECT",VERTEX,{"derivedFrom":[subQ1,subQ0]});Q9=makeQuery(id+"F15.imprint","IMPRINT",FACE,{"disambiguationData":[TD([[makeQuery(id+"F15.imprint","IMPRINT",EDGE,{"disambiguationData":[TD([[subQ2,1.0]])],"derivedFrom":subQ1}),-1.0]])]});}
            var Q10;
            {var subQ4=sQuery(id+"F15.wireOp",EDGE,"E133");var subQ5=sQuery(id+"F15.wireOp",EDGE,"E115");var subQ6=makeQuery(id+"F15.imprint","INTERSECT",VERTEX,{"derivedFrom":[subQ5,subQ4]});Q10=makeQuery(id+"F15.imprint","IMPRINT",FACE,{"disambiguationData":[TD([[makeQuery(id+"F15.imprint","IMPRINT",EDGE,{"disambiguationData":[TD([[subQ6,-1.0]])],"derivedFrom":subQ5}),-1.0]])]});}
            var Q11;
            {var subQ5=sQuery(id+"F15.wireOp",EDGE,"E146");Q11=makeQuery(id+"F15.imprint","IMPRINT",FACE,{"disambiguationData":[TD([[makeQuery(id+"F15.imprint","IMPRINT",EDGE,{"derivedFrom":subQ5}),1.0]])]});}
            var Q12;
            {var subQ4=sQuery(id+"F15.wireOp",EDGE,"E120.0");var subQ6=sQuery(id+"F15.wireOp",EDGE,"E133");var subQ7=makeQuery(id+"F15.imprint","INTERSECT",VERTEX,{"derivedFrom":[subQ4,subQ6]});Q12=makeQuery(id+"F15.imprint","IMPRINT",FACE,{"disambiguationData":[TD([[makeQuery(id+"F15.imprint","IMPRINT",EDGE,{"disambiguationData":[TD([[subQ7,-1.0]])],"derivedFrom":subQ4}),1.0]])]});}
            var Q13;
            {var subQ0=sQuery(id+"F15.wireOp",EDGE,"E146");Q13=makeQuery(id+"F15.imprint","IMPRINT",FACE,{"disambiguationData":[TD([[makeQuery(id+"F15.imprint","IMPRINT",EDGE,{"derivedFrom":subQ0}),-1.0]])]});}
            var Q14;
            {var subQ0=sQuery(id+"F15.wireOp",EDGE,"E132");var subQ1=sQuery(id+"F15.wireOp",EDGE,"E115");var subQ2=makeQuery(id+"F15.imprint","INTERSECT",VERTEX,{"derivedFrom":[subQ1,subQ0]});Q14=makeQuery(id+"F15.imprint","IMPRINT",FACE,{"disambiguationData":[TD([[makeQuery(id+"F15.imprint","IMPRINT",EDGE,{"disambiguationData":[TD([[subQ2,1.0]])],"derivedFrom":subQ1}),-1.0]])]});}
            var Q15;
            {var subQ0=sQuery(id+"F15.wireOp",EDGE,"E136.0");var subQ1=sQuery(id+"F15.wireOp",EDGE,"E132");var subQ2=makeQuery(id+"F15.imprint","INTERSECT",VERTEX,{"derivedFrom":[subQ1,subQ0]});Q15=makeQuery(id+"F15.imprint","IMPRINT",FACE,{"disambiguationData":[TD([[makeQuery(id+"F15.imprint","IMPRINT",EDGE,{"disambiguationData":[TD([[subQ2,-1.0]])],"derivedFrom":subQ1}),1.0]])]});}
            var Q16;
            {var subQ0=sQuery(id+"F15.wireOp",EDGE,"E132");var subQ1=sQuery(id+"F15.wireOp",EDGE,"E120.0");var subQ2=makeQuery(id+"F15.imprint","INTERSECT",VERTEX,{"derivedFrom":[subQ1,subQ0]});Q16=makeQuery(id+"F15.imprint","IMPRINT",FACE,{"disambiguationData":[TD([[makeQuery(id+"F15.imprint","IMPRINT",EDGE,{"disambiguationData":[TD([[subQ2,1.0]])],"derivedFrom":subQ1}),1.0]])]});}
            var Q17;
            {var subQ0=sQuery(id+"F15.wireOp",EDGE,"E131");var subQ1=sQuery(id+"F15.wireOp",EDGE,"E115");var subQ2=makeQuery(id+"F15.imprint","INTERSECT",VERTEX,{"derivedFrom":[subQ1,subQ0]});Q17=makeQuery(id+"F15.imprint","IMPRINT",FACE,{"disambiguationData":[TD([[makeQuery(id+"F15.imprint","IMPRINT",EDGE,{"disambiguationData":[TD([[subQ2,1.0]])],"derivedFrom":subQ1}),-1.0]])]});}
            var Q18;
            {var subQ0=sQuery(id+"F15.wireOp",EDGE,"E137.0");var subQ1=sQuery(id+"F15.wireOp",EDGE,"E131");var subQ2=makeQuery(id+"F15.imprint","INTERSECT",VERTEX,{"derivedFrom":[subQ1,subQ0]});Q18=makeQuery(id+"F15.imprint","IMPRINT",FACE,{"disambiguationData":[TD([[makeQuery(id+"F15.imprint","IMPRINT",EDGE,{"disambiguationData":[TD([[subQ2,-1.0]])],"derivedFrom":subQ1}),-1.0]])]});}
            var Q19;
            {var subQ0=sQuery(id+"F15.wireOp",EDGE,"E131");var subQ1=sQuery(id+"F15.wireOp",EDGE,"E120.0");var subQ2=makeQuery(id+"F15.imprint","INTERSECT",VERTEX,{"derivedFrom":[subQ1,subQ0]});Q19=makeQuery(id+"F15.imprint","IMPRINT",FACE,{"disambiguationData":[TD([[makeQuery(id+"F15.imprint","IMPRINT",EDGE,{"disambiguationData":[TD([[subQ2,1.0]])],"derivedFrom":subQ1}),1.0]])]});}
            var Q20;
            {var subQ0=sQuery(id+"F15.wireOp",EDGE,"E131");var subQ1=sQuery(id+"F15.wireOp",EDGE,"E115");var subQ2=makeQuery(id+"F15.imprint","INTERSECT",VERTEX,{"derivedFrom":[subQ1,subQ0]});Q20=makeQuery(id+"F15.imprint","IMPRINT",FACE,{"disambiguationData":[TD([[makeQuery(id+"F15.imprint","IMPRINT",EDGE,{"disambiguationData":[TD([[subQ2,-1.0]])],"derivedFrom":subQ1}),-1.0]])]});}
            var Q21;
            {var subQ0=sQuery(id+"F15.wireOp",EDGE,"E137.0");var subQ1=sQuery(id+"F15.wireOp",EDGE,"E131");var subQ2=makeQuery(id+"F15.imprint","INTERSECT",VERTEX,{"derivedFrom":[subQ1,subQ0]});Q21=makeQuery(id+"F15.imprint","IMPRINT",FACE,{"disambiguationData":[TD([[makeQuery(id+"F15.imprint","IMPRINT",EDGE,{"disambiguationData":[TD([[subQ2,-1.0]])],"derivedFrom":subQ1}),1.0]])]});}
            var Q22;
            {var subQ0=sQuery(id+"F15.wireOp",EDGE,"E131");var subQ1=sQuery(id+"F15.wireOp",EDGE,"E120.0");var subQ2=makeQuery(id+"F15.imprint","INTERSECT",VERTEX,{"derivedFrom":[subQ1,subQ0]});Q22=makeQuery(id+"F15.imprint","IMPRINT",FACE,{"disambiguationData":[TD([[makeQuery(id+"F15.imprint","IMPRINT",EDGE,{"disambiguationData":[TD([[subQ2,-1.0]])],"derivedFrom":subQ1}),1.0]])]});}
            var Q23;
            {var subQ4=sQuery(id+"F15.wireOp",EDGE,"E115");var subQ6=sQuery(id+"F15.wireOp",EDGE,"E130");var subQ8=makeQuery(id+"F15.imprint","INTERSECT",VERTEX,{"derivedFrom":[subQ4,subQ6]});Q23=makeQuery(id+"F15.imprint","IMPRINT",FACE,{"disambiguationData":[TD([[makeQuery(id+"F15.imprint","IMPRINT",EDGE,{"disambiguationData":[TD([[subQ8,1.0]])],"derivedFrom":subQ4}),-1.0]])]});}
            var Q24;
            {var subQ0=sQuery(id+"F15.wireOp",EDGE,"E149");Q24=makeQuery(id+"F15.imprint","IMPRINT",FACE,{"disambiguationData":[TD([[makeQuery(id+"F15.imprint","IMPRINT",EDGE,{"derivedFrom":subQ0}),-1.0]])]});}
            var Q25;
            {var subQ4=sQuery(id+"F15.wireOp",EDGE,"E130");var subQ6=sQuery(id+"F15.wireOp",EDGE,"E120.0");var subQ7=makeQuery(id+"F15.imprint","INTERSECT",VERTEX,{"derivedFrom":[subQ6,subQ4]});Q25=makeQuery(id+"F15.imprint","IMPRINT",FACE,{"disambiguationData":[TD([[makeQuery(id+"F15.imprint","IMPRINT",EDGE,{"disambiguationData":[TD([[subQ7,1.0]])],"derivedFrom":subQ6}),1.0]])]});}
            var Q26;
            {var subQ5=sQuery(id+"F15.wireOp",EDGE,"E149");Q26=makeQuery(id+"F15.imprint","IMPRINT",FACE,{"disambiguationData":[TD([[makeQuery(id+"F15.imprint","IMPRINT",EDGE,{"derivedFrom":subQ5}),1.0]])]});}
            var Q27;
            {var subQ5=sQuery(id+"F15.wireOp",EDGE,"E145");Q27=makeQuery(id+"F15.imprint","IMPRINT",FACE,{"disambiguationData":[TD([[makeQuery(id+"F15.imprint","IMPRINT",EDGE,{"derivedFrom":subQ5}),1.0]])]});}
            extrude(context, id + "F17", {"entities" : qUnion([Q0, Q1, Q2, Q3, Q4, Q5, Q6, Q7, Q8, Q9, Q10, Q11, Q12, Q13, Q14, Q15, Q16, Q17, Q18, Q19, Q20, Q21, Q22, Q23, Q24, Q25, Q26, Q27]), "depth" : 22.35 * mm, "offsetDistance" : 25.4 * mm});
        }
        {
            var Q0;
            {var subQ0=sQuery(id+"F15.wireOp",EDGE,"E144");Q0=makeQuery(id+"F15.imprint","IMPRINT",FACE,{"disambiguationData":[TD([[makeQuery(id+"F15.imprint","IMPRINT",EDGE,{"derivedFrom":subQ0}),1.0]])]});}
            var Q1;
            {var subQ0=sQuery(id+"F15.wireOp",EDGE,"E146");Q1=makeQuery(id+"F15.imprint","IMPRINT",FACE,{"disambiguationData":[TD([[makeQuery(id+"F15.imprint","IMPRINT",EDGE,{"derivedFrom":subQ0}),-1.0]])]});}
            var Q2;
            {var subQ0=sQuery(id+"F15.wireOp",EDGE,"E149");Q2=makeQuery(id+"F15.imprint","IMPRINT",FACE,{"disambiguationData":[TD([[makeQuery(id+"F15.imprint","IMPRINT",EDGE,{"derivedFrom":subQ0}),-1.0]])]});}
            extrude(context, id + "F18", {"entities" : qUnion([Q0, Q1, Q2]), "operationType" : NewBodyOperationType.ADD, "oppositeDirection" : true, "depth" : 5.7 * mm, "offsetDistance" : 25.4 * mm});
        }
        {
            var Q0;
            Q0=qCreatedBy(makeId("Top.planeOp"),FACE);
            var sketch = newSketch(context, id + "F19", { "sketchPlane" : qUnion([Q0])});
            skLineSegment(sketch, "E152", {"start": v(-8.24, 42.23) * mm, "end": v(-8.24, 67.63) * mm});
            skLineSegment(sketch, "E153.0", {"start": v(-8.24, 64.58) * mm, "end": v(8.24, 64.58) * mm});
            skLineSegment(sketch, "E154", {"start": v(8.24, 67.63) * mm, "end": v(8.24, 42.23) * mm});
            skLineSegment(sketch, "E155.0", {"start": v(-5.75, 42.23) * mm, "end": v(5.75, 42.23) * mm});
            skLineSegment(sketch, "E156.0", {"start": v(-8.24, 42.23) * mm, "end": v(8.24, 42.23) * mm});
            skLineSegment(sketch, "E157", {"start": v(-4.57, 42.23) * mm, "end": v(-4.57, 64.58) * mm});
            skLineSegment(sketch, "E158", {"start": v(0, 42.23) * mm, "end": v(0, 64.58) * mm, "construction": true});
            skLineSegment(sketch, "E159.MirrorCS", {"start": v(4.57, 42.23) * mm, "end": v(4.57, 64.58) * mm});
            skLineSegment(sketch, "E160", {"start": v(-4.57, 44.8) * mm, "end": v(0, 44.8) * mm});
            skLineSegment(sketch, "E161.bottom", {"start": v(-4.57, 45.4) * mm, "end": v(4.57, 45.4) * mm});
            skLineSegment(sketch, "E161.top", {"start": v(-4.57, 48.58) * mm, "end": v(4.57, 48.58) * mm});
            skLineSegment(sketch, "E161.left", {"start": v(-4.57, 45.4) * mm, "end": v(-4.57, 48.58) * mm});
            skLineSegment(sketch, "E161.right", {"start": v(4.57, 45.4) * mm, "end": v(4.57, 48.58) * mm});
            skLineSegment(sketch, "E162.left", {"start": v(-4.57, 51.12) * mm, "end": v(-4.57, 54.93) * mm});
            skLineSegment(sketch, "E162.right", {"start": v(4.57, 51.12) * mm, "end": v(4.57, 57.2) * mm});
            skLineSegment(sketch, "E163.bottom", {"start": v(-4.57, 51.12) * mm, "end": v(4.57, 51.12) * mm});
            skLineSegment(sketch, "E163.top", {"start": v(-4.57, 54.3) * mm, "end": v(4.57, 54.3) * mm});
            skLineSegment(sketch, "E163.left", {"start": v(-4.57, 51.12) * mm, "end": v(-4.57, 54.3) * mm});
            skLineSegment(sketch, "E163.right", {"start": v(4.57, 51.12) * mm, "end": v(4.57, 54.3) * mm});
            skLineSegment(sketch, "E164", {"start": v(0, 48.58) * mm, "end": v(0, 51.12) * mm});
            skLineSegment(sketch, "E165.bottom", {"start": v(-4.57, 56.83) * mm, "end": v(4.57, 56.83) * mm});
            skLineSegment(sketch, "E165.top", {"start": v(-4.57, 60) * mm, "end": v(4.57, 60) * mm});
            skLineSegment(sketch, "E165.left", {"start": v(-4.57, 56.83) * mm, "end": v(-4.57, 60) * mm});
            skLineSegment(sketch, "E165.right", {"start": v(4.57, 56.83) * mm, "end": v(4.57, 60) * mm});
            skLineSegment(sketch, "E166", {"start": v(-1.97, 54.3) * mm, "end": v(-1.97, 56.83) * mm, "construction": true});
            skLineSegment(sketch, "E167", {"start": v(0, 42.23) * mm, "end": v(0, 45.4) * mm});
            skLineSegment(sketch, "E168", {"start": v(0.9, 42.23) * mm, "end": v(0.9, 45.4) * mm});
            skSolve(sketch);
        }
        {
            var Q0;
            {var subQ0=sQuery(id+"F19.wireOp",EDGE,"E161.left");Q0=makeQuery(id+"F19.imprint","IMPRINT",FACE,{"disambiguationData":[TD([[makeQuery(id+"F19.imprint","IMPRINT",EDGE,{"derivedFrom":subQ0}),-1.0]])]});}
            var Q1;
            Q1=makeQuery(id+"F19.imprint","IMPRINT",FACE,{"disambiguationData":[TD([[makeQuery(id+"F19.imprint","IMPRINT",EDGE,{"derivedFrom":sQuery(id+"F19.wireOp",EDGE,"E163.top")}),-1.0]])]});
            var Q2;
            {var subQ1=sQuery(id+"F19.wireOp",EDGE,"E165.bottom");Q2=makeQuery(id+"F19.imprint","IMPRINT",FACE,{"disambiguationData":[TD([[makeQuery(id+"F19.imprint","IMPRINT",EDGE,{"derivedFrom":subQ1}),1.0]])]});}
            var Q3;
            Q3=sQuery(id+"F19.wireOp",EDGE,"E161.right");
            var Q4;
            Q4=sQuery(id+"F19.wireOp",EDGE,"E161.bottom");
            var Q5;
            Q5=sQuery(id+"F19.wireOp",EDGE,"E161.left");
            var Q6;
            Q6=sQuery(id+"F19.wireOp",EDGE,"E161.top");
            extrude(context, id + "F20", {"entities" : qUnion([Q0, Q1, Q2]), "operationType" : NewBodyOperationType.REMOVE, "surfaceEntities" : qUnion([Q3, Q4, Q5, Q6]), "depth" : 25.4 * mm, "offsetDistance" : 25.4 * mm});
        }
        {
            var Q0;
            Q0=qCreatedBy(makeId("Right.planeOp"),FACE);
            var sketch = newSketch(context, id + "F21", { "sketchPlane" : qUnion([Q0])});
            skLineSegment(sketch, "E169", {"start": v(42.23, 22.21) * mm, "end": v(67.63, 22.21) * mm});
            skLineSegment(sketch, "E170", {"start": v(67.63, 5.73) * mm, "end": v(42.23, 5.73) * mm});
            skLineSegment(sketch, "E171.0", {"start": v(64.58, 22.21) * mm, "end": v(64.58, 5.73) * mm});
            skLineSegment(sketch, "E172.0", {"start": v(42.23, 19.72) * mm, "end": v(42.23, 8.22) * mm});
            skLineSegment(sketch, "E173", {"start": v(64.58, 13.97) * mm, "end": v(42.23, 13.97) * mm, "construction": true});
            skLineSegment(sketch, "E174", {"start": v(42.23, 18.54) * mm, "end": v(64.58, 18.54) * mm, "construction": true});
            skLineSegment(sketch, "E175", {"start": v(45.4, 18.54) * mm, "end": v(45.4, 13.97) * mm, "construction": true});
            skLineSegment(sketch, "E176", {"start": v(42.23, 16.67) * mm, "end": v(45.4, 16.67) * mm, "construction": true});
            skLineSegment(sketch, "E177.MirrorCS", {"start": v(42.23, 9.4) * mm, "end": v(64.58, 9.4) * mm, "construction": true});
            skLineSegment(sketch, "E178.bottom", {"start": v(45.4, 18.54) * mm, "end": v(48.58, 18.54) * mm});
            skLineSegment(sketch, "E178.top", {"start": v(45.4, 9.4) * mm, "end": v(48.58, 9.4) * mm});
            skLineSegment(sketch, "E178.left", {"start": v(45.4, 18.54) * mm, "end": v(45.4, 9.4) * mm});
            skLineSegment(sketch, "E178.right", {"start": v(48.58, 18.54) * mm, "end": v(48.58, 9.4) * mm});
            skLineSegment(sketch, "E179.bottom", {"start": v(51.12, 18.54) * mm, "end": v(54.3, 18.54) * mm});
            skLineSegment(sketch, "E179.top", {"start": v(51.12, 9.4) * mm, "end": v(54.3, 9.4) * mm});
            skLineSegment(sketch, "E179.left", {"start": v(51.12, 18.54) * mm, "end": v(51.12, 9.4) * mm});
            skLineSegment(sketch, "E179.right", {"start": v(54.3, 18.54) * mm, "end": v(54.3, 9.4) * mm});
            skLineSegment(sketch, "E180", {"start": v(48.58, 15.67) * mm, "end": v(51.12, 15.67) * mm, "construction": true});
            skLineSegment(sketch, "E181.bottom", {"start": v(56.83, 18.54) * mm, "end": v(60, 18.54) * mm});
            skLineSegment(sketch, "E181.top", {"start": v(56.83, 9.4) * mm, "end": v(60, 9.4) * mm});
            skLineSegment(sketch, "E181.left", {"start": v(56.83, 18.54) * mm, "end": v(56.83, 9.4) * mm});
            skLineSegment(sketch, "E181.right", {"start": v(60, 18.54) * mm, "end": v(60, 9.4) * mm});
            skLineSegment(sketch, "E182", {"start": v(54.3, 15.96) * mm, "end": v(56.83, 15.96) * mm, "construction": true});
            skLineSegment(sketch, "E183", {"start": v(60, 13.97) * mm, "end": v(64.58, 13.97) * mm});
            skLineSegment(sketch, "E184", {"start": v(60, 13.97) * mm, "end": v(62.3, 13.97) * mm});
            skLineSegment(sketch, "E185", {"start": v(60, 14.73) * mm, "end": v(64.58, 14.73) * mm, "construction": true});
            skSolve(sketch);
        }
        {
            var Q0;
            Q0=makeQuery(id+"F21.imprint","IMPRINT",FACE,{"disambiguationData":[TD([[makeQuery(id+"F21.imprint","IMPRINT",EDGE,{"derivedFrom":sQuery(id+"F21.wireOp",EDGE,"E178.bottom")}),-1.0]])]});
            var Q1;
            Q1=makeQuery(id+"F21.imprint","IMPRINT",FACE,{"disambiguationData":[TD([[makeQuery(id+"F21.imprint","IMPRINT",EDGE,{"derivedFrom":sQuery(id+"F21.wireOp",EDGE,"E179.bottom")}),-1.0]])]});
            var Q2;
            Q2=makeQuery(id+"F21.imprint","IMPRINT",FACE,{"disambiguationData":[TD([[makeQuery(id+"F21.imprint","IMPRINT",EDGE,{"derivedFrom":sQuery(id+"F21.wireOp",EDGE,"E181.top")}),1.0]])]});
            extrude(context, id + "F22", {"entities" : qUnion([Q0, Q1, Q2]), "operationType" : NewBodyOperationType.REMOVE, "endBound" : BoundingType.SYMMETRIC, "oppositeDirection" : true, "depth" : 50.8 * mm, "offsetDistance" : 25.4 * mm});
        }
        {
            var Q0;
            Q0=makeQuery(id+"F17.opExtrude","CAP_FACE",FACE,{"disambiguationData":[OSD([sQuery(id+"F15.wireOp",EDGE,"E115"),sQuery(id+"F15.wireOp",EDGE,"E120.0")])],"isStart":false});
            var sketch = newSketch(context, id + "F23", { "sketchPlane" : qUnion([Q0])});
            skCircle(sketch, "E186.0", {"center": v(0, 13.97) * mm, "radius": 8.24 * mm});
            skLineSegment(sketch, "E187.0.0", {"start": v(-16.83, 0) * mm, "end": v(16.83, 0) * mm});
            skLineSegment(sketch, "E187.0.1", {"start": v(16.83, 0) * mm, "end": v(16.83, 25.4) * mm});
            skLineSegment(sketch, "E187.0.2", {"start": v(16.83, 25.4) * mm, "end": v(-16.83, 25.4) * mm});
            skLineSegment(sketch, "E187.0.3", {"start": v(-16.83, 25.4) * mm, "end": v(-16.83, 0) * mm});
            skCircle(sketch, "E188.0", {"center": v(0, 13.97) * mm, "radius": 4.69 * mm});
            skSolve(sketch);
        }
        {
            var Q0;
            Q0=makeQuery(id+"F23.imprint","IMPRINT",FACE,{"disambiguationData":[TD([[makeQuery(id+"F23.imprint","IMPRINT",EDGE,{"derivedFrom":sQuery(id+"F23.wireOp",EDGE,"E186.0")}),1.0]])]});
            var Q1;
            Q1=makeQuery(id+"F23.imprint","IMPRINT",FACE,{"disambiguationData":[TD([[makeQuery(id+"F23.imprint","IMPRINT",EDGE,{"derivedFrom":sQuery(id+"F23.wireOp",EDGE,"E188.0")}),1.0]])]});
            var Q2;
            Q2=makeQuery(id+"F23.imprint","IMPRINT",FACE,{"disambiguationData":[TD([[makeQuery(id+"F23.imprint","IMPRINT",EDGE,{"derivedFrom":sQuery(id+"F23.wireOp",EDGE,"E188.0")}),-1.0]])]});
            extrude(context, id + "F24", {"entities" : qUnion([Q0, Q1, Q2]), "operationType" : NewBodyOperationType.ADD, "depth" : 2.54 * mm, "offsetDistance" : 25.4 * mm});
        }
        {
            var Q0;
            Q0=makeQuery(id+"F23.imprint","IMPRINT",FACE,{"disambiguationData":[TD([[makeQuery(id+"F23.imprint","IMPRINT",EDGE,{"derivedFrom":sQuery(id+"F23.wireOp",EDGE,"E188.0")}),1.0]])]});
            extrude(context, id + "F25", {"entities" : qUnion([Q0]), "operationType" : NewBodyOperationType.REMOVE, "endBound" : BoundingType.UP_TO_NEXT, "depth" : 25.4 * mm, "offsetDistance" : 25.4 * mm});
        }
        {
            var Q0;
            Q0=makeQuery(id+"F9.opExtrude","CAP_FACE",FACE,{"disambiguationData":[OSD([sQuery(id+"F0.wireOp",EDGE,"E1.0"),sQuery(id+"F0.wireOp",EDGE,"E1.1"),sQuery(id+"F0.wireOp",EDGE,"E1.2"),sQuery(id+"F0.wireOp",EDGE,"E1.3")])],"isStart":false});
            var Q1;
            Q1=makeQuery(id+"F9.opExtrude","SWEPT_EDGE",EDGE,{"disambiguationData":[OSD([sQuery(id+"F0.wireOp",EDGE,"E1.0"),sQuery(id+"F0.wireOp",EDGE,"E1.1")])]});
            var Q2;
            Q2=makeQuery(id+"F9.opExtrude","SWEPT_EDGE",EDGE,{"disambiguationData":[OSD([sQuery(id+"F0.wireOp",EDGE,"E1.1"),sQuery(id+"F0.wireOp",EDGE,"E1.2")])]});
            var Q3;
            Q3=makeQuery(id+"F9.opExtrude","SWEPT_EDGE",EDGE,{"disambiguationData":[OSD([sQuery(id+"F0.wireOp",EDGE,"E1.2"),sQuery(id+"F0.wireOp",EDGE,"E1.3")])]});
            var Q4;
            Q4=makeQuery(id+"F9.opExtrude","SWEPT_EDGE",EDGE,{"disambiguationData":[OSD([sQuery(id+"F0.wireOp",EDGE,"E1.0"),sQuery(id+"F0.wireOp",EDGE,"E1.3")])]});
            fillet(context, id + "F26", {"entities" : qUnion([Q0, Q1, Q2, Q3, Q4]), "radius" : 2.54 * mm, "tangentPropagation" : true, "allowEdgeOverflow" : false});
        }
        {
            var Q0;
            Q0=makeQuery(id+"F1.opExtrude","SWEPT_EDGE",EDGE,{"disambiguationData":[OSD([sQuery(id+"F0.wireOp",EDGE,"E1.0"),sQuery(id+"F0.wireOp",EDGE,"E1.1")])]});
            var Q1;
            Q1=makeQuery(id+"F1.opExtrude","SWEPT_EDGE",EDGE,{"disambiguationData":[OSD([sQuery(id+"F0.wireOp",EDGE,"E1.1"),sQuery(id+"F0.wireOp",EDGE,"E1.2")])]});
            var Q2;
            Q2=makeQuery(id+"F1.opExtrude","SWEPT_EDGE",EDGE,{"disambiguationData":[OSD([sQuery(id+"F0.wireOp",EDGE,"E1.0"),sQuery(id+"F0.wireOp",EDGE,"E1.3")])]});
            var Q3;
            Q3=makeQuery(id+"F1.opExtrude","SWEPT_EDGE",EDGE,{"disambiguationData":[OSD([sQuery(id+"F0.wireOp",EDGE,"E1.2"),sQuery(id+"F0.wireOp",EDGE,"E1.3")])]});
            fillet(context, id + "F27", {"entities" : qUnion([Q0, Q1, Q2, Q3]), "radius" : 2.54 * mm, "tangentPropagation" : true, "allowEdgeOverflow" : false});
        }
        {
            var Q0;
            Q0=makeQuery(id+"F1.opExtrude","CAP_FACE",FACE,{"disambiguationData":[OSD([sQuery(id+"F0.wireOp",EDGE,"E1.0"),sQuery(id+"F0.wireOp",EDGE,"E1.1"),sQuery(id+"F0.wireOp",EDGE,"E1.2"),sQuery(id+"F0.wireOp",EDGE,"E1.3")])],"isStart":true});
            fillet(context, id + "F28", {"entities" : qUnion([Q0]), "radius" : 2.54 * mm, "tangentPropagation" : true, "allowEdgeOverflow" : false});
        }
    });
